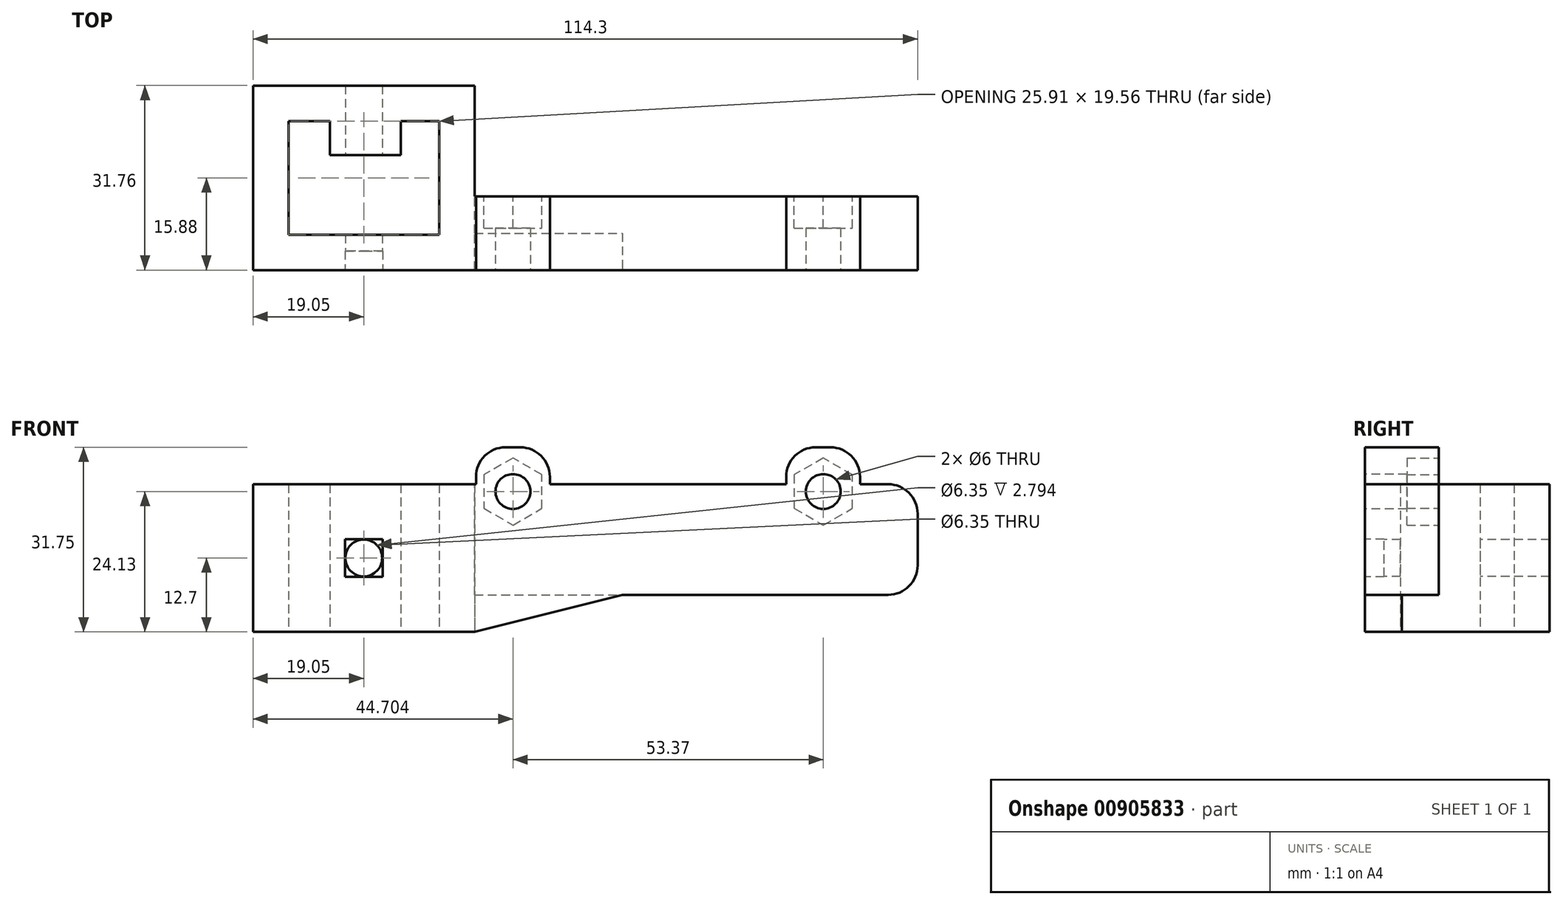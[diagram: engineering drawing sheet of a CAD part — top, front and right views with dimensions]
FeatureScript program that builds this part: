
annotation { "Feature Type Name" : "Feature", "Feature Type Description" : "" }
export const myFeature = defineFeature(function(context is Context, id is Id, definition is map)
    precondition{}
    {
        {
            var Q0;
            Q0=qCreatedBy(makeId("Top.planeOp"),FACE);
            var sketch = newSketch(context, id + "F0", { "sketchPlane" : qUnion([Q0])});
            skLineSegment(sketch, "E0.bottom", {"start": v(12.95, -9.78) * mm, "end": v(-12.95, -9.78) * mm});
            skLineSegment(sketch, "E0.top", {"start": v(12.95, 9.78) * mm, "end": v(6.35, 9.78) * mm});
            skLineSegment(sketch, "E0.left", {"start": v(12.95, -9.78) * mm, "end": v(12.95, 9.78) * mm});
            skLineSegment(sketch, "E0.right", {"start": v(-12.95, -9.78) * mm, "end": v(-12.95, 9.78) * mm});
            skPoint(sketch, "E0.middle", {"position": v(0, 0) * mm});
            skLineSegment(sketch, "E1.0", {"start": v(19.05, 15.88) * mm, "end": v(-19.05, 15.87) * mm});
            skLineSegment(sketch, "E1.1", {"start": v(19.05, -15.87) * mm, "end": v(19.05, 15.88) * mm});
            skLineSegment(sketch, "E1.2", {"start": v(19.05, -15.87) * mm, "end": v(-19.05, -15.88) * mm});
            skLineSegment(sketch, "E1.3", {"start": v(-19.05, -15.88) * mm, "end": v(-19.05, 15.87) * mm});
            skLineSegment(sketch, "E2.top", {"start": v(-5.84, 3.94) * mm, "end": v(6.35, 3.94) * mm});
            skLineSegment(sketch, "E2.left", {"start": v(-5.84, 9.78) * mm, "end": v(-5.84, 3.94) * mm});
            skLineSegment(sketch, "E2.right", {"start": v(6.35, 9.78) * mm, "end": v(6.35, 3.94) * mm});
            skLineSegment(sketch, "E3.trimOffspring", {"start": v(-5.84, 9.78) * mm, "end": v(-12.95, 9.78) * mm});
            skLineSegment(sketch, "E4", {"start": v(-19.05, 15.87) * mm, "end": v(-19.05, -15.88) * mm});
            skSolve(sketch);
        }
        {
            var Q0;
            Q0=makeQuery(id+"F0.imprint","IMPRINT",FACE,{"disambiguationData":[TD([[makeQuery(id+"F0.imprint","IMPRINT",EDGE,{"derivedFrom":sQuery(id+"F0.wireOp",EDGE,"E0.bottom")}),1.0]])]});
            extrude(context, id + "F1", {"entities" : qUnion([Q0]), "depth" : 25.4 * mm, "offsetDistance" : 25.4 * mm, "symmetric" : true});
        }
        {
            var Q0;
            Q0=makeQuery(id+"F1.opExtrude","SWEPT_FACE",FACE,{"disambiguationData":[OSD([sQuery(id+"F0.wireOp",EDGE,"E1.2")])]});
            var sketch = newSketch(context, id + "F2", { "sketchPlane" : qUnion([Q0])});
            skCircle(sketch, "E5", {"center": v(0, 0) * mm, "radius": 3.18 * mm});
            skSolve(sketch);
        }
        {
            var Q0;
            Q0=makeQuery(id+"F2.imprint","IMPRINT",FACE,{"disambiguationData":[TD([[makeQuery(id+"F2.imprint","IMPRINT",EDGE,{"derivedFrom":sQuery(id+"F2.wireOp",EDGE,"E5")}),1.0]])]});
            extrude(context, id + "F3", {"entities" : qUnion([Q0]), "operationType" : NewBodyOperationType.REMOVE, "endBound" : BoundingType.THROUGH_ALL, "oppositeDirection" : true, "depth" : 25.4 * mm, "offsetDistance" : 25.4 * mm});
        }
        {
            var Q0;
            Q0=makeQuery(id+"F1.opExtrude","SWEPT_FACE",FACE,{"disambiguationData":[OSD([sQuery(id+"F0.wireOp",EDGE,"E1.2")])]});
            var sketch = newSketch(context, id + "F4", { "sketchPlane" : qUnion([Q0])});
            skLineSegment(sketch, "E6.bottom", {"start": v(3.24, -3.24) * mm, "end": v(-3.24, -3.24) * mm});
            skLineSegment(sketch, "E6.top", {"start": v(3.24, 3.24) * mm, "end": v(-3.24, 3.24) * mm});
            skLineSegment(sketch, "E6.left", {"start": v(3.24, -3.24) * mm, "end": v(3.24, 3.24) * mm});
            skLineSegment(sketch, "E6.right", {"start": v(-3.24, -3.24) * mm, "end": v(-3.24, 3.24) * mm});
            skPoint(sketch, "E6.middle", {"position": v(0, 0) * mm});
            skSolve(sketch);
        }
        {
            var Q0;
            Q0 = qSketchRegion(id + "F4", true);
            extrude(context, id + "F5", {"entities" : qUnion([Q0]), "operationType" : NewBodyOperationType.REMOVE, "oppositeDirection" : true, "depth" : 3.3 * mm, "offsetDistance" : 25.4 * mm});
        }
        {
            var Q0;
            Q0=makeQuery(id+"F1.opExtrude","CAP_FACE",FACE,{"disambiguationData":[OSD([sQuery(id+"F0.wireOp",EDGE,"E0.bottom"),sQuery(id+"F0.wireOp",EDGE,"E0.top"),sQuery(id+"F0.wireOp",EDGE,"E0.left"),sQuery(id+"F0.wireOp",EDGE,"E0.right"),sQuery(id+"F0.wireOp",EDGE,"E1.0"),sQuery(id+"F0.wireOp",EDGE,"E1.1"),sQuery(id+"F0.wireOp",EDGE,"E1.2"),sQuery(id+"F0.wireOp",EDGE,"E2.top"),sQuery(id+"F0.wireOp",EDGE,"E2.left"),sQuery(id+"F0.wireOp",EDGE,"E2.right"),sQuery(id+"F0.wireOp",EDGE,"E3.trimOffspring"),sQuery(id+"F0.wireOp",EDGE,"E4")])],"isStart":false});
            var sketch = newSketch(context, id + "F6", { "sketchPlane" : qUnion([Q0])});
            skLineSegment(sketch, "E7.bottom", {"start": v(19.05, -3.17) * mm, "end": v(95.25, -3.17) * mm});
            skLineSegment(sketch, "E7.top", {"start": v(19.05, -15.87) * mm, "end": v(95.25, -15.87) * mm});
            skLineSegment(sketch, "E7.left", {"start": v(19.05, -3.17) * mm, "end": v(19.05, -15.87) * mm});
            skLineSegment(sketch, "E7.right", {"start": v(95.25, -3.17) * mm, "end": v(95.25, -15.87) * mm});
            skSolve(sketch);
        }
        {
            var Q0;
            Q0=makeQuery(id+"F6.imprint","IMPRINT",FACE,{"disambiguationData":[TD([[makeQuery(id+"F6.imprint","IMPRINT",EDGE,{"derivedFrom":sQuery(id+"F6.wireOp",EDGE,"E7.bottom")}),-1.0]])]});
            extrude(context, id + "F7", {"entities" : qUnion([Q0]), "operationType" : NewBodyOperationType.ADD, "oppositeDirection" : true, "depth" : 19.05 * mm, "offsetDistance" : 25.4 * mm});
        }
        {
            var Q0;
            Q0=makeQuery(id+"F7.boolean.opBoolean","MERGE",FACE,{"derivedFrom":[makeQuery(id+"F1.opExtrude","SWEPT_FACE",FACE,{"disambiguationData":[OSD([sQuery(id+"F0.wireOp",EDGE,"E1.2")])]}),makeQuery(id+"F7.opExtrude","SWEPT_FACE",FACE,{"disambiguationData":[OSD([sQuery(id+"F6.wireOp",EDGE,"E7.top")])]})]});
            var sketch = newSketch(context, id + "F8", { "sketchPlane" : qUnion([Q0])});
            skLineSegment(sketch, "E8", {"start": v(19.05, -12.7) * mm, "end": v(19.05, -6.35) * mm});
            skLineSegment(sketch, "E9", {"start": v(19.05, -6.35) * mm, "end": v(44.45, -6.35) * mm});
            skLineSegment(sketch, "E10", {"start": v(44.45, -6.35) * mm, "end": v(19.05, -12.7) * mm});
            skSolve(sketch);
        }
        {
            var Q0;
            Q0 = qSketchRegion(id + "F8", true);
            extrude(context, id + "F9", {"entities" : qUnion([Q0]), "operationType" : NewBodyOperationType.ADD, "oppositeDirection" : true, "depth" : 6.35 * mm, "offsetDistance" : 25.4 * mm});
        }
        {
            var Q0;
            Q0=makeQuery(id+"F7.boolean.opBoolean","MERGE",FACE,{"derivedFrom":[makeQuery(id+"F1.opExtrude","CAP_FACE",FACE,{"disambiguationData":[OSD([sQuery(id+"F0.wireOp",EDGE,"E0.bottom"),sQuery(id+"F0.wireOp",EDGE,"E0.top"),sQuery(id+"F0.wireOp",EDGE,"E0.left"),sQuery(id+"F0.wireOp",EDGE,"E0.right"),sQuery(id+"F0.wireOp",EDGE,"E1.0"),sQuery(id+"F0.wireOp",EDGE,"E1.1"),sQuery(id+"F0.wireOp",EDGE,"E1.2"),sQuery(id+"F0.wireOp",EDGE,"E2.top"),sQuery(id+"F0.wireOp",EDGE,"E2.left"),sQuery(id+"F0.wireOp",EDGE,"E2.right"),sQuery(id+"F0.wireOp",EDGE,"E3.trimOffspring"),sQuery(id+"F0.wireOp",EDGE,"E4")])],"isStart":false}),makeQuery(id+"F7.opExtrude","CAP_FACE",FACE,{"disambiguationData":[OSD([sQuery(id+"F6.wireOp",EDGE,"E7.bottom"),sQuery(id+"F6.wireOp",EDGE,"E7.top"),sQuery(id+"F6.wireOp",EDGE,"E7.left"),sQuery(id+"F6.wireOp",EDGE,"E7.right")])],"isStart":true})]});
            var sketch = newSketch(context, id + "F10", { "sketchPlane" : qUnion([Q0])});
            skLineSegment(sketch, "E11.bottom", {"start": v(32, -15.87) * mm, "end": v(19.3, -15.87) * mm});
            skLineSegment(sketch, "E11.top", {"start": v(32, -3.17) * mm, "end": v(19.3, -3.17) * mm});
            skLineSegment(sketch, "E11.left", {"start": v(32, -15.87) * mm, "end": v(32, -3.17) * mm});
            skLineSegment(sketch, "E11.right", {"start": v(19.3, -15.87) * mm, "end": v(19.3, -3.17) * mm});
            skPoint(sketch, "E11.middle", {"position": v(25.65, -9.52) * mm});
            skLineSegment(sketch, "E12.bottom", {"start": v(85.34, -15.87) * mm, "end": v(72.64, -15.87) * mm});
            skLineSegment(sketch, "E12.top", {"start": v(85.34, -3.18) * mm, "end": v(72.64, -3.18) * mm});
            skLineSegment(sketch, "E12.left", {"start": v(85.34, -15.87) * mm, "end": v(85.34, -3.17) * mm});
            skLineSegment(sketch, "E12.right", {"start": v(72.64, -15.87) * mm, "end": v(72.64, -3.17) * mm});
            skPoint(sketch, "E12.middle", {"position": v(79, -9.52) * mm});
            skSolve(sketch);
        }
        {
            var Q0;
            Q0 = qSketchRegion(id + "F10", true);
            extrude(context, id + "F11", {"entities" : qUnion([Q0]), "operationType" : NewBodyOperationType.ADD, "depth" : 6.35 * mm, "offsetDistance" : 25.4 * mm});
        }
        {
            var Q0;
            Q0=makeQuery(id+"F11.opExtrude","CAP_EDGE",EDGE,{"disambiguationData":[OSD([sQuery(id+"F10.wireOp",EDGE,"E11.right")])],"isStart":false});
            var Q1;
            Q1=makeQuery(id+"F11.opExtrude","CAP_EDGE",EDGE,{"disambiguationData":[OSD([sQuery(id+"F10.wireOp",EDGE,"E11.left")])],"isStart":false});
            var Q2;
            Q2=makeQuery(id+"F11.opExtrude","CAP_EDGE",EDGE,{"disambiguationData":[OSD([sQuery(id+"F10.wireOp",EDGE,"E12.right")])],"isStart":false});
            var Q3;
            Q3=makeQuery(id+"F11.opExtrude","CAP_EDGE",EDGE,{"disambiguationData":[OSD([sQuery(id+"F10.wireOp",EDGE,"E12.left")])],"isStart":false});
            fillet(context, id + "F12", {"entities" : qUnion([Q0, Q1, Q2, Q3]), "radius" : 5.08 * mm, "tangentPropagation" : true, "allowEdgeOverflow" : false});
        }
        {
            var Q0;
            Q0=makeQuery(id+"F11.boolean.opBoolean","MERGE",FACE,{"derivedFrom":[makeQuery(id+"F9.boolean.opBoolean","MERGE",FACE,{"derivedFrom":[makeQuery(id+"F7.boolean.opBoolean","MERGE",FACE,{"derivedFrom":[makeQuery(id+"F1.opExtrude","SWEPT_FACE",FACE,{"disambiguationData":[OSD([sQuery(id+"F0.wireOp",EDGE,"E1.2")])]}),makeQuery(id+"F7.opExtrude","SWEPT_FACE",FACE,{"disambiguationData":[OSD([sQuery(id+"F6.wireOp",EDGE,"E7.top")])]})]}),makeQuery(id+"F9.opExtrude","CAP_FACE",FACE,{"disambiguationData":[OSD([sQuery(id+"F8.wireOp",EDGE,"E8"),sQuery(id+"F8.wireOp",EDGE,"E9"),sQuery(id+"F8.wireOp",EDGE,"E10")])],"isStart":true})]}),makeQuery(id+"F11.opExtrude","SWEPT_FACE",FACE,{"disambiguationData":[OSD([sQuery(id+"F10.wireOp",EDGE,"E11.bottom")])]}),makeQuery(id+"F11.opExtrude","SWEPT_FACE",FACE,{"disambiguationData":[OSD([sQuery(id+"F10.wireOp",EDGE,"E12.bottom")])]})]});
            var sketch = newSketch(context, id + "F13", { "sketchPlane" : qUnion([Q0])});
            skCircle(sketch, "E13", {"center": v(25.65, 11.43) * mm, "radius": 3 * mm});
            skCircle(sketch, "E14", {"center": v(79.02, 11.43) * mm, "radius": 3 * mm});
            skSolve(sketch);
        }
        {
            var Q0;
            Q0 = qSketchRegion(id + "F13", true);
            extrude(context, id + "F14", {"entities" : qUnion([Q0]), "operationType" : NewBodyOperationType.REMOVE, "endBound" : BoundingType.THROUGH_ALL, "oppositeDirection" : true, "depth" : 25.4 * mm, "offsetDistance" : 25.4 * mm});
        }
        {
            var Q0;
            Q0=makeQuery(id+"F11.boolean.opBoolean","MERGE",FACE,{"derivedFrom":[makeQuery(id+"F7.opExtrude","SWEPT_FACE",FACE,{"disambiguationData":[OSD([sQuery(id+"F6.wireOp",EDGE,"E7.bottom")])]}),makeQuery(id+"F11.opExtrude","SWEPT_FACE",FACE,{"disambiguationData":[OSD([sQuery(id+"F10.wireOp",EDGE,"E11.top")])]}),makeQuery(id+"F11.opExtrude","SWEPT_FACE",FACE,{"disambiguationData":[OSD([sQuery(id+"F10.wireOp",EDGE,"E12.top")])]})]});
            var sketch = newSketch(context, id + "F15", { "sketchPlane" : qUnion([Q0])});
            skCircle(sketch, "E15.cCircle", {"center": v(-79.02, 11.43) * mm, "radius": 5.77 * mm, "construction": true});
            skLineSegment(sketch, "E15.0", {"start": v(-79.02, 5.66) * mm, "end": v(-84.02, 8.54) * mm});
            skLineSegment(sketch, "E15.1", {"start": v(-84.02, 8.54) * mm, "end": v(-84.02, 14.32) * mm});
            skLineSegment(sketch, "E15.2", {"start": v(-84.02, 14.32) * mm, "end": v(-79.02, 17.2) * mm});
            skLineSegment(sketch, "E15.3", {"start": v(-79.02, 17.2) * mm, "end": v(-74.02, 14.32) * mm});
            skLineSegment(sketch, "E15.4", {"start": v(-74.02, 14.32) * mm, "end": v(-74.02, 8.54) * mm});
            skLineSegment(sketch, "E15.5", {"start": v(-74.02, 8.54) * mm, "end": v(-79.02, 5.66) * mm});
            skCircle(sketch, "E16.cCircle", {"center": v(-25.65, 11.43) * mm, "radius": 5.77 * mm, "construction": true});
            skLineSegment(sketch, "E16.0", {"start": v(-25.65, 5.66) * mm, "end": v(-30.65, 8.54) * mm});
            skLineSegment(sketch, "E16.1", {"start": v(-30.65, 8.54) * mm, "end": v(-30.65, 14.32) * mm});
            skLineSegment(sketch, "E16.2", {"start": v(-30.65, 14.32) * mm, "end": v(-25.65, 17.2) * mm});
            skLineSegment(sketch, "E16.3", {"start": v(-25.65, 17.2) * mm, "end": v(-20.65, 14.32) * mm});
            skLineSegment(sketch, "E16.4", {"start": v(-20.65, 14.32) * mm, "end": v(-20.65, 8.54) * mm});
            skLineSegment(sketch, "E16.5", {"start": v(-20.65, 8.54) * mm, "end": v(-25.65, 5.66) * mm});
            skSolve(sketch);
        }
        {
            var Q0;
            Q0=makeQuery(id+"F15.imprint","IMPRINT",FACE,{"disambiguationData":[TD([[makeQuery(id+"F15.imprint","IMPRINT",EDGE,{"derivedFrom":sQuery(id+"F15.wireOp",EDGE,"E15.0")}),-1.0]])]});
            var Q1;
            Q1=makeQuery(id+"F15.imprint","IMPRINT",FACE,{"disambiguationData":[TD([[makeQuery(id+"F15.imprint","IMPRINT",EDGE,{"derivedFrom":sQuery(id+"F15.wireOp",EDGE,"E16.0")}),-1.0]])]});
            extrude(context, id + "F16", {"entities" : qUnion([Q0, Q1]), "operationType" : NewBodyOperationType.REMOVE, "oppositeDirection" : true, "depth" : 5.5 * mm, "offsetDistance" : 25.4 * mm});
        }
        {
            var Q0;
            Q0=makeQuery(id+"F7.opExtrude","CAP_EDGE",EDGE,{"disambiguationData":[OSD([sQuery(id+"F6.wireOp",EDGE,"E7.right")])],"isStart":true});
            var Q1;
            Q1=makeQuery(id+"F7.opExtrude","CAP_EDGE",EDGE,{"disambiguationData":[OSD([sQuery(id+"F6.wireOp",EDGE,"E7.right")])],"isStart":false});
            fillet(context, id + "F17", {"entities" : qUnion([Q0, Q1]), "radius" : 5.08 * mm, "tangentPropagation" : true, "allowEdgeOverflow" : false});
        }
    });
